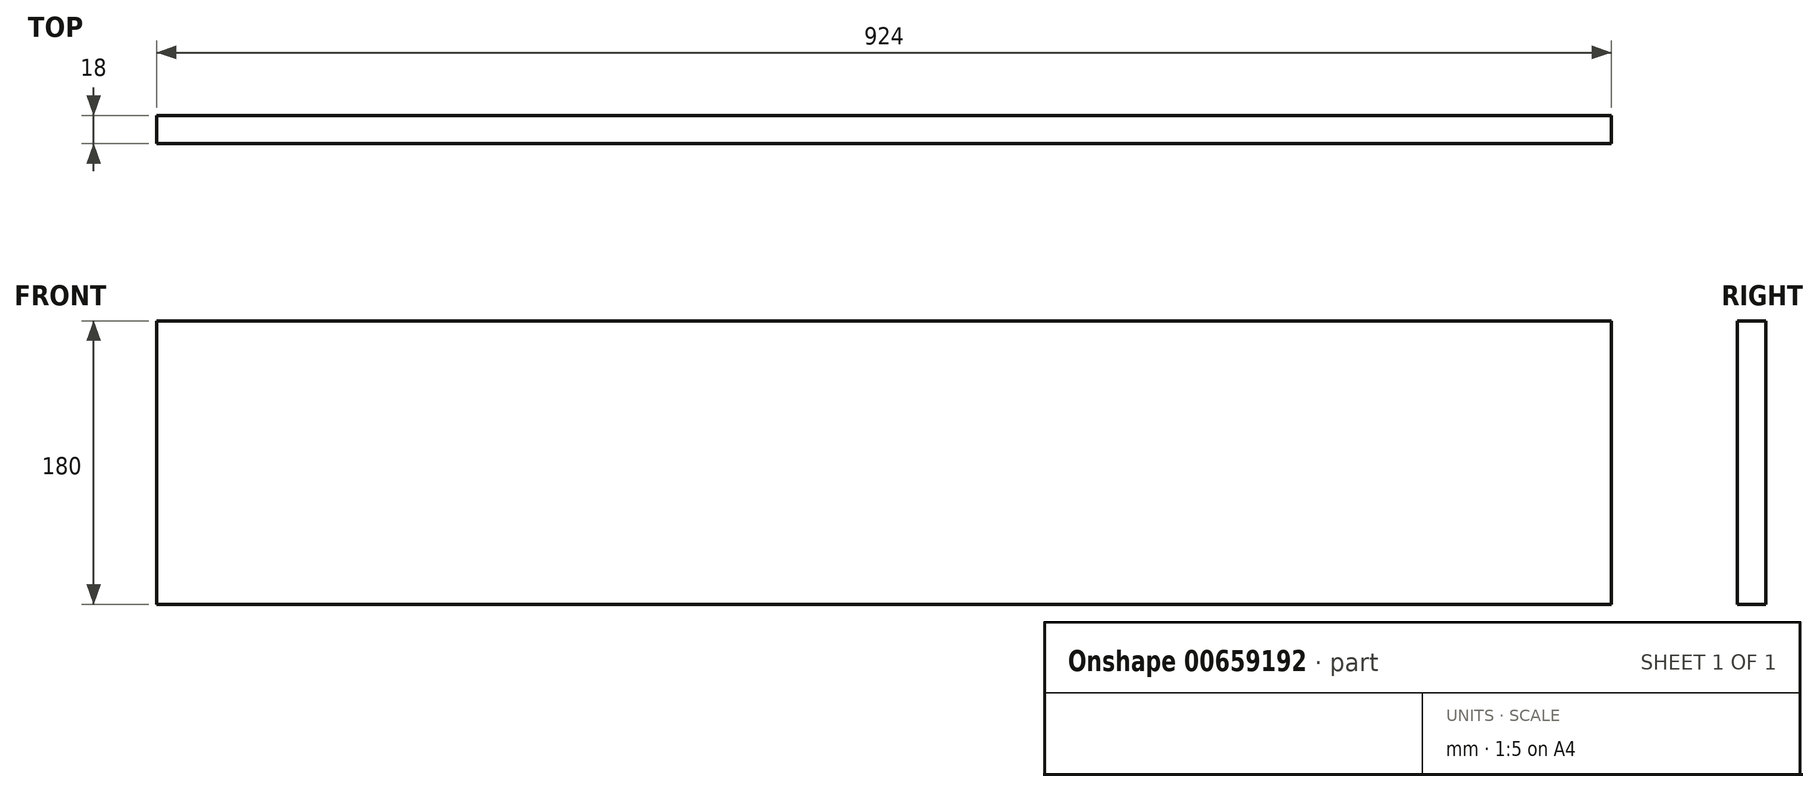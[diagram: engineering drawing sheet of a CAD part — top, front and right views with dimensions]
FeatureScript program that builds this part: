
annotation { "Feature Type Name" : "Feature", "Feature Type Description" : "" }
export const myFeature = defineFeature(function(context is Context, id is Id, definition is map)
    precondition{}
    {
        {
            var Q0;
            Q0=qCreatedBy(makeId("Front.planeOp"),FACE);
            var sketch = newSketch(context, id + "F0", { "sketchPlane" : qUnion([Q0])});
            skLineSegment(sketch, "E0.bottom", {"start": v(-462, -90) * mm, "end": v(462, -90) * mm});
            skLineSegment(sketch, "E0.top", {"start": v(-462, 90) * mm, "end": v(462, 90) * mm});
            skLineSegment(sketch, "E0.left", {"start": v(-462, -90) * mm, "end": v(-462, 90) * mm});
            skLineSegment(sketch, "E0.right", {"start": v(462, -90) * mm, "end": v(462, 90) * mm});
            skPoint(sketch, "E0.middle", {"position": v(0, 0) * mm});
            skSolve(sketch);
        }
        {
            var Q0;
            Q0=makeQuery(id+"F0.imprint","IMPRINT",FACE,{"disambiguationData":[TD([[makeQuery(id+"F0.imprint","IMPRINT",EDGE,{"derivedFrom":sQuery(id+"F0.wireOp",EDGE,"E0.bottom")}),1.0]])]});
            extrude(context, id + "F1", {"entities" : qUnion([Q0]), "endBound" : BoundingType.SYMMETRIC, "depth" : 18 * mm, "offsetDistance" : 25 * mm});
        }
    });
